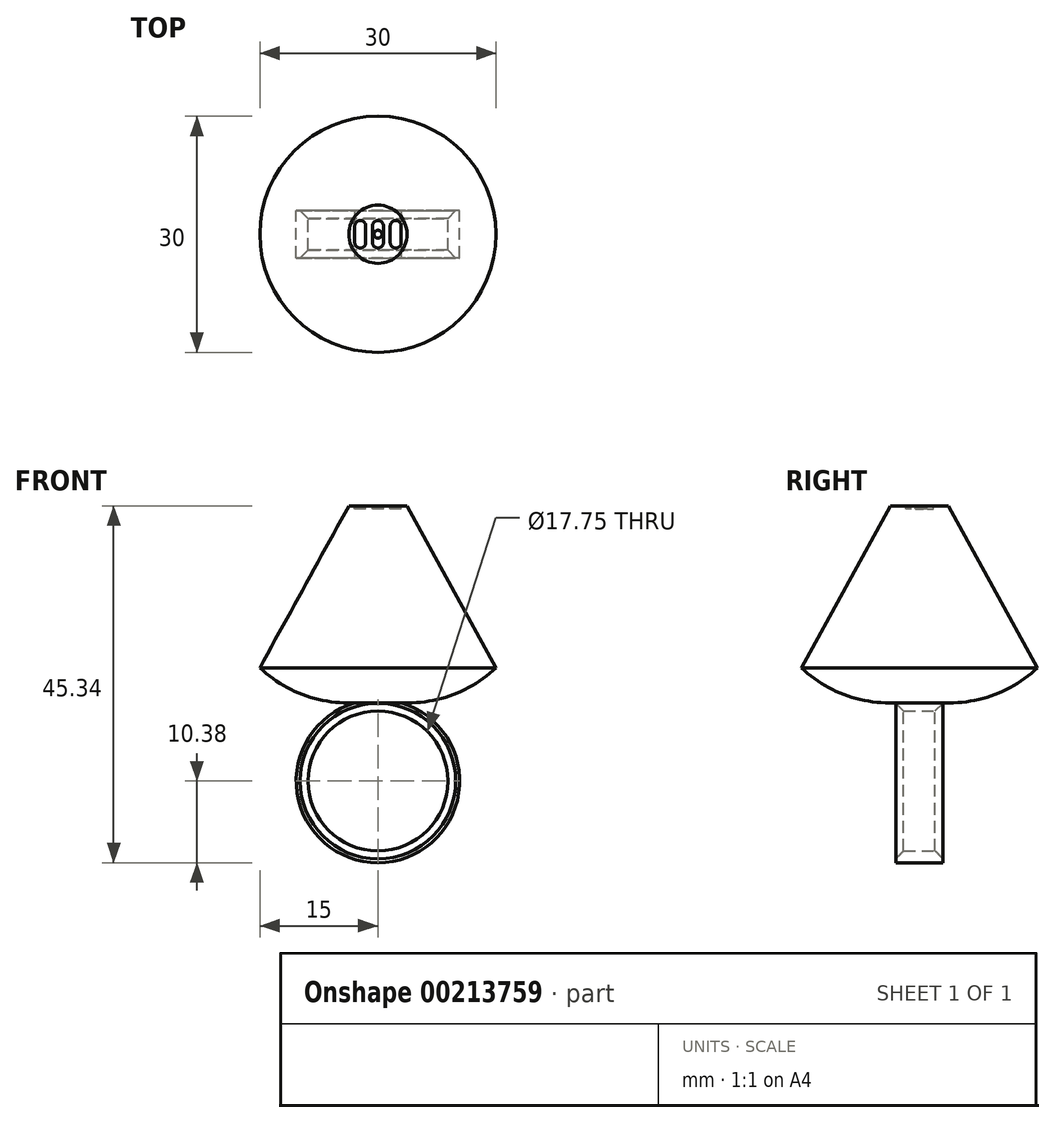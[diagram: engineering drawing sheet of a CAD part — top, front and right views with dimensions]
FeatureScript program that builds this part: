
annotation { "Feature Type Name" : "Feature", "Feature Type Description" : "" }
export const myFeature = defineFeature(function(context is Context, id is Id, definition is map)
    precondition{}
    {
        {
            var Q0;
            Q0=qCreatedBy(makeId("Front.planeOp"),FACE);
            var sketch = newSketch(context, id + "F0", { "sketchPlane" : qUnion([Q0])});
            skCircle(sketch, "E0", {"center": v(0, 0) * mm, "radius": 8.88 * mm});
            skCircle(sketch, "E1.0", {"center": v(0, 0) * mm, "radius": 10.38 * mm});
            skLineSegment(sketch, "E2", {"start": v(0, 9.96) * mm, "end": v(2.9, 9.96) * mm});
            skArc(sketch, "E3", {"start": v(2.9, 9.96) * mm, "mid": v(9.4, 10.93) * mm, "end": v(15, 14.38) * mm});
            skLineSegment(sketch, "E4", {"start": v(15, 14.38) * mm, "end": v(3.7, 34.96) * mm});
            skLineSegment(sketch, "E5", {"start": v(3.7, 34.96) * mm, "end": v(0, 34.96) * mm});
            skPoint(sketch, "E6", {"position": v(0, 9.96) * mm});
            skPoint(sketch, "E7.orphan", {"position": v(-2.9, 9.96) * mm});
            skLineSegment(sketch, "E8", {"start": v(0, 34.96) * mm, "end": v(0, 9.96) * mm});
            skSolve(sketch);
        }
        {
            var Q0;
            Q0=qCreatedBy(makeId("Top.planeOp"),FACE);
            var sketch = newSketch(context, id + "F1", { "sketchPlane" : qUnion([Q0])});
            skCircle(sketch, "E9", {"center": v(0, 0) * mm, "radius": 4.62 * mm});
            skSolve(sketch);
        }
        {
            var Q0;
            {var subQ1=sQuery(id+"F0.wireOp",EDGE,"E3");Q0=makeQuery(id+"F0.imprint","IMPRINT",FACE,{"disambiguationData":[TD([[makeQuery(id+"F0.imprint","IMPRINT",EDGE,{"derivedFrom":subQ1}),1.0]])]});}
            var Q1;
            Q1=sQuery(id+"F1.wireOp",EDGE,"E9");
            revolve(context, id + "F2", {"entities" : qUnion([Q0]), "axis" : qUnion([Q1]), "revolveType" : RevolveType.FULL});
        }
        {
            var Q0;
            Q0=makeQuery(id+"F0.imprint","IMPRINT",FACE,{"disambiguationData":[TD([[makeQuery(id+"F0.imprint","IMPRINT",EDGE,{"derivedFrom":sQuery(id+"F0.wireOp",EDGE,"E0")}),-1.0]])]});
            var Q1;
            {var subQ0=sQuery(id+"F0.wireOp",EDGE,"E2");Q1=makeQuery(id+"F0.imprint","IMPRINT",FACE,{"disambiguationData":[TD([[makeQuery(id+"F0.imprint","IMPRINT",EDGE,{"derivedFrom":subQ0}),1.0]])]});}
            extrude(context, id + "F3", {"entities" : qUnion([Q0, Q1]), "operationType" : NewBodyOperationType.ADD, "depth" : 3 * mm, "hasSecondDirection" : true, "secondDirectionOppositeDirection" : true, "secondDirectionDepth" : 3 * mm});
        }
        {
            var Q0;
            Q0=makeQuery(id+"F3.opExtrude","CAP_EDGE",EDGE,{"disambiguationData":[OSD([sQuery(id+"F0.wireOp",EDGE,"E0")])],"isStart":false});
            var Q1;
            Q1=makeQuery(id+"F3.opExtrude","CAP_EDGE",EDGE,{"disambiguationData":[OSD([sQuery(id+"F0.wireOp",EDGE,"E0")])],"isStart":true});
            chamfer(context, id + "F4", {"entities" : qUnion([Q0, Q1]), "width" : 1 * mm, "tangentPropagation" : true});
        }
        {
            var Q0;
            Q0=makeQuery(id+"F2.opRevolve","SWEPT_FACE",FACE,{"disambiguationData":[OSD([sQuery(id+"F0.wireOp",EDGE,"E5")])]});
            var sketch = newSketch(context, id + "F5", { "sketchPlane" : qUnion([Q0])});
            skLineSegment(sketch, "E10.bottom", {"start": v(-0.7, 1.05) * mm, "end": v(-0.7, -1.04) * mm});
            skArc(sketch, "E11.filletArc", {"start": v(0.7, 1.05) * mm, "mid": v(0.5, 1.55) * mm, "end": v(0, 1.75) * mm});
            skArc(sketch, "E12.filletArc", {"start": v(0, 1.75) * mm, "mid": v(-0.5, 1.55) * mm, "end": v(-0.7, 1.05) * mm});
            skArc(sketch, "E13.filletArc", {"start": v(0, -1.74) * mm, "mid": v(0.5, -1.53) * mm, "end": v(0.7, -1.04) * mm});
            skArc(sketch, "E14.filletArc", {"start": v(-0.7, -1.04) * mm, "mid": v(-0.5, -1.53) * mm, "end": v(0, -1.74) * mm});
            skLineSegment(sketch, "E15.bottom", {"start": v(-2.95, 1.05) * mm, "end": v(-2.95, -1.04) * mm});
            skLineSegment(sketch, "E15.top", {"start": v(-1.55, 1.05) * mm, "end": v(-1.55, -1.04) * mm});
            skArc(sketch, "E16.filletArc", {"start": v(-1.55, 1.05) * mm, "mid": v(-1.75, 1.55) * mm, "end": v(-2.25, 1.75) * mm});
            skArc(sketch, "E17.filletArc", {"start": v(-2.25, 1.75) * mm, "mid": v(-2.74, 1.55) * mm, "end": v(-2.95, 1.05) * mm});
            skArc(sketch, "E18.filletArc", {"start": v(-2.25, -1.74) * mm, "mid": v(-1.75, -1.53) * mm, "end": v(-1.55, -1.04) * mm});
            skArc(sketch, "E19.filletArc", {"start": v(-2.95, -1.04) * mm, "mid": v(-2.74, -1.53) * mm, "end": v(-2.25, -1.74) * mm});
            skLineSegment(sketch, "E20", {"start": v(0.7, 1.05) * mm, "end": v(0.7, -1.04) * mm});
            skCircle(sketch, "E21", {"center": v(0, 0) * mm, "radius": 0.5 * mm});
            skLineSegment(sketch, "E22.bottom", {"start": v(1.56, 1.05) * mm, "end": v(1.56, -1.04) * mm});
            skLineSegment(sketch, "E22.top", {"start": v(2.96, 1.05) * mm, "end": v(2.96, -1.04) * mm});
            skArc(sketch, "E23.filletArc", {"start": v(2.96, 1.05) * mm, "mid": v(2.75, 1.55) * mm, "end": v(2.26, 1.75) * mm});
            skArc(sketch, "E24.filletArc", {"start": v(2.26, 1.75) * mm, "mid": v(1.76, 1.55) * mm, "end": v(1.56, 1.05) * mm});
            skArc(sketch, "E25.filletArc", {"start": v(2.26, -1.74) * mm, "mid": v(2.75, -1.53) * mm, "end": v(2.96, -1.04) * mm});
            skArc(sketch, "E26.filletArc", {"start": v(1.56, -1.04) * mm, "mid": v(1.76, -1.53) * mm, "end": v(2.26, -1.74) * mm});
            skSolve(sketch);
        }
        {
            var Q0;
            Q0=makeQuery(id+"F5.imprint","IMPRINT",FACE,{"disambiguationData":[TD([[makeQuery(id+"F5.imprint","IMPRINT",EDGE,{"derivedFrom":sQuery(id+"F5.wireOp",EDGE,"E10.bottom")}),1.0]])]});
            var Q1;
            Q1=makeQuery(id+"F5.imprint","IMPRINT",FACE,{"disambiguationData":[TD([[makeQuery(id+"F5.imprint","IMPRINT",EDGE,{"derivedFrom":sQuery(id+"F5.wireOp",EDGE,"E15.bottom")}),1.0]])]});
            var Q2;
            Q2=makeQuery(id+"F5.imprint","IMPRINT",FACE,{"disambiguationData":[TD([[makeQuery(id+"F5.imprint","IMPRINT",EDGE,{"derivedFrom":sQuery(id+"F5.wireOp",EDGE,"E22.bottom")}),1.0]])]});
            extrude(context, id + "F6", {"entities" : qUnion([Q0, Q1, Q2]), "operationType" : NewBodyOperationType.REMOVE, "oppositeDirection" : true, "depth" : .43 * mm, "offsetDistance" : 25 * mm});
        }
    });
